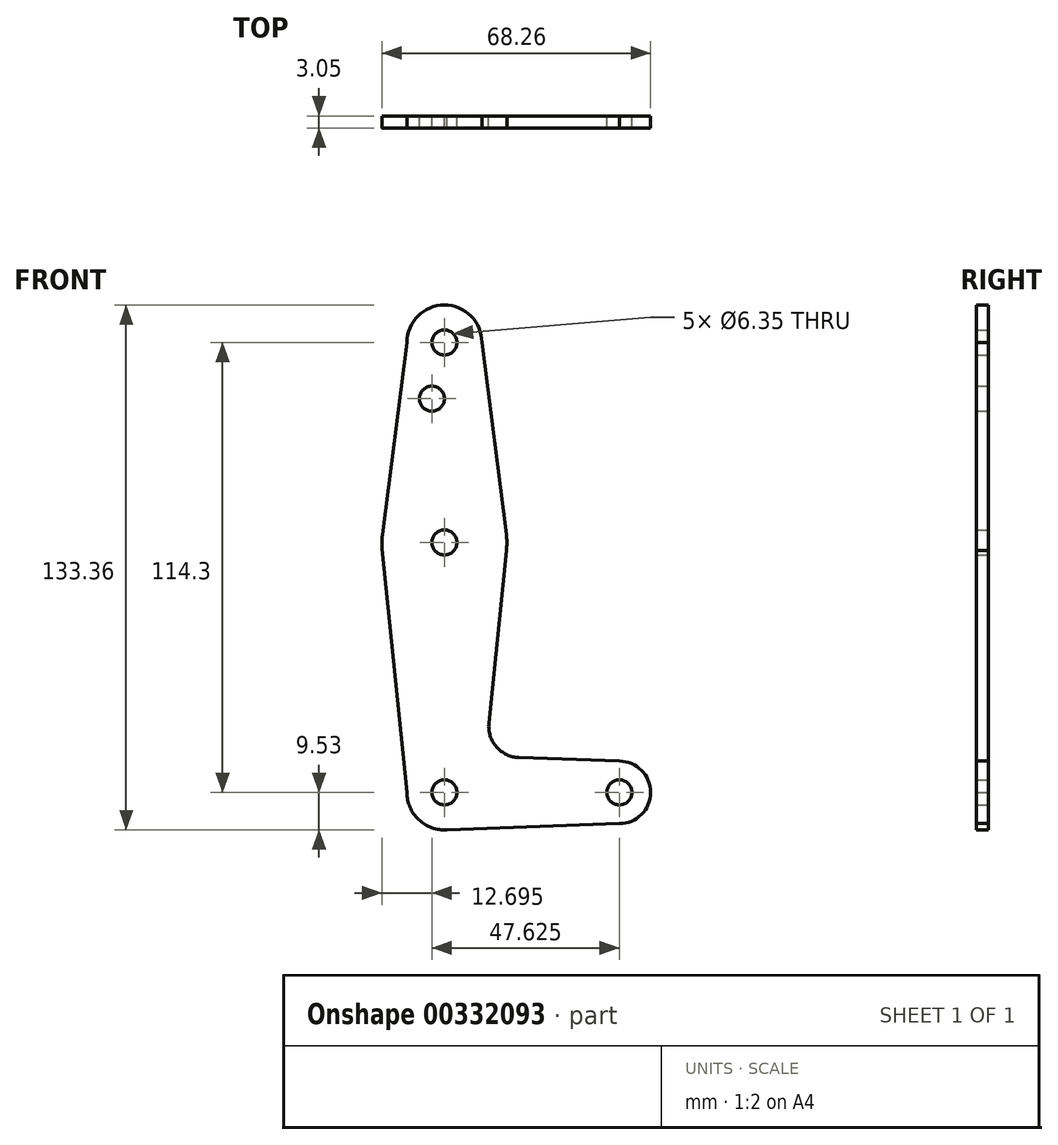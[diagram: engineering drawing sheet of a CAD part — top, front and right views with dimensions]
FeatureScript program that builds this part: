
annotation { "Feature Type Name" : "Feature", "Feature Type Description" : "" }
export const myFeature = defineFeature(function(context is Context, id is Id, definition is map)
    precondition{}
    {
        {
            var Q0;
            Q0=qCreatedBy(makeId("Front.planeOp"),FACE);
            var sketch = newSketch(context, id + "F0", { "sketchPlane" : qUnion([Q0])});
            skLineSegment(sketch, "E0", {"start": v(0, 0) * mm, "end": v(0, 114.3) * mm, "construction": true});
            skLineSegment(sketch, "E1", {"start": v(0, 0) * mm, "end": v(44.45, 0) * mm, "construction": true});
            skCircle(sketch, "E2", {"center": v(0, 0) * mm, "radius": 9.52 * mm});
            skCircle(sketch, "E3", {"center": v(0, 114.3) * mm, "radius": 9.53 * mm});
            skCircle(sketch, "E4", {"center": v(44.45, 0) * mm, "radius": 7.94 * mm});
            skCircle(sketch, "E5", {"center": v(0, 63.5) * mm, "radius": 15.88 * mm});
            skLineSegment(sketch, "E6", {"start": v(9.53, 114.3) * mm, "end": v(15.75, 65.5) * mm});
            skLineSegment(sketch, "E7", {"start": v(-9.53, 114.3) * mm, "end": v(-15.75, 65.5) * mm});
            skLineSegment(sketch, "E8", {"start": v(11.3, 17.6) * mm, "end": v(15.75, 61.5) * mm});
            skLineSegment(sketch, "E9", {"start": v(-9.52, 0) * mm, "end": v(-15.8, 61.9) * mm});
            skLineSegment(sketch, "E10", {"start": v(18.93, 8.85) * mm, "end": v(44.45, 7.94) * mm});
            skLineSegment(sketch, "E11", {"start": v(0, -9.52) * mm, "end": v(44.45, -7.94) * mm});
            skCircle(sketch, "E12", {"center": v(0, 114.3) * mm, "radius": 3.18 * mm});
            skCircle(sketch, "E13", {"center": v(0, 63.5) * mm, "radius": 3.18 * mm});
            skCircle(sketch, "E14", {"center": v(0, 0) * mm, "radius": 3.18 * mm});
            skCircle(sketch, "E15", {"center": v(44.45, 0) * mm, "radius": 3.18 * mm});
            skCircle(sketch, "E16", {"center": v(-3.18, 100.03) * mm, "radius": 3.18 * mm});
            skArc(sketch, "E17.filletArc", {"start": v(11.3, 17.6) * mm, "mid": v(13.22, 11.57) * mm, "end": v(18.93, 8.85) * mm});
            skSolve(sketch);
        }
        {
            var Q0;
            Q0 = qSketchRegion(id + "F0", true);
            extrude(context, id + "F1", {"entities" : qUnion([Q0]), "depth" : 3.05 * mm});
        }
    });
